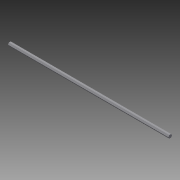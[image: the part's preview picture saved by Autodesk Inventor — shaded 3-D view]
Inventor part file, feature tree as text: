
AUTODESK INVENTOR PART (.ipt)
format: ipt  version: 2015 SP1 (Build 190203100, 203)  size: 78,848 bytes
history: native  units: in
note: dims shown in document units (in); Inventor stores cm internally (conversion verified against a paired STEP export)
features: extrude x1, sketch x1
ambient origin geometry x8: Origin, YZ Plane, XZ Plane, XY Plane, X Axis, Y Axis, Z Axis, Center Point
bodies: Solid1 (feature_tree)
feature tree (2):
  extrude  "Extrusion1"  Depth=0.5in
  sketch  "Sketch1"  dims[d0=0.5in d1=0.5in d2=0.5in d3=0.25in d4=120.0deg d5=120.0deg d6=0.25in d7=0.25in d8=25.5in d9=0.0in]
